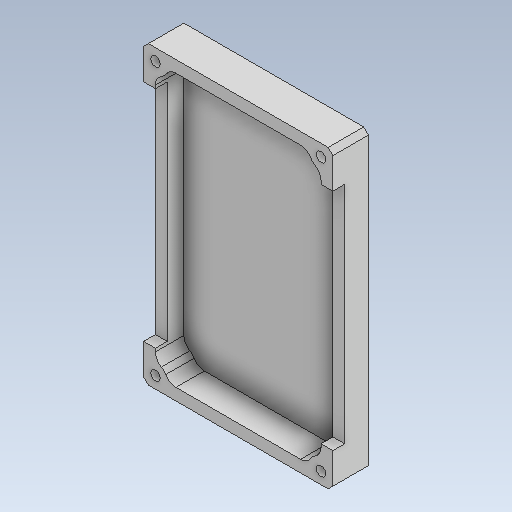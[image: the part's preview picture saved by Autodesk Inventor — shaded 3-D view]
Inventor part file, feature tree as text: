
AUTODESK INVENTOR PART (.ipt)
format: ipt  version: 2020 (Build 240168000, 168)  size: 218,112 bytes
history: native  units: mm
features: extrude x4, sketch x4, projected_geometry x2, hole x1, fillet x1, chamfer x1
ambient origin geometry x8: Origin, YZ Plane, XZ Plane, XY Plane, X Axis, Y Axis, Z Axis, Center Point
bodies: Solid1 (feature_tree)
feature tree (13):
  extrude  "Extrusion1"  Depth=125.0mm
  extrude  "Extrusion2"  Depth=5.0mm
  hole  "Hole1"  [1 undecoded]
  extrude  "Extrusion3"  Depth=5.0mm TaperAngle=0.0deg
  fillet  "Fillet1"  Radius=5.0mm
  extrude  "Extrusion5"  Depth=5.0mm TaperAngle=0.0deg
  chamfer  "Chamfer1"  Distance=115.0mm
  sketch  "Sketch1"  dims[d0=80.0mm d1=125.0mm]
  sketch  "Sketch2"  dims[d2=15.0mm d3=0.0mm d4=5.0mm]
  projected_geometry  "Projected Loop1"
  sketch  "Sketch3"  dims[d5=12.0mm d6=0.0mm]
  projected_geometry  "Projected Loop2"
  sketch  "Sketch6"  dims[d9=4.0mm d10=6.0mm d11=4.0mm d12=2.0mm d13=90.0deg d14=8.0mm d15=20.594885mm d16=10.0mm d19=27.0mm d20=0.0mm d21=5.0mm d25=50.0mm d26=0.0mm d27=115.0mm d28=70.0mm d29=2.0mm d30=2.0mm d31=45.0deg d32=5.0mm d33=1.34mm d34=1.34mm]
note: 1 required parameter value undecoded (feature->parameter linkage not recoverable at this tier; creation-order binding heuristic only, values carry confidence <= 0.55)
